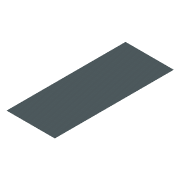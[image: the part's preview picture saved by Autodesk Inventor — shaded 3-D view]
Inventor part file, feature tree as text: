
AUTODESK INVENTOR PART (.ipt)
format: ipt  version: unknown  size: 158,720 bytes
history: native  units: in
note: dims shown in document units (in); Inventor stores cm internally (conversion verified against a paired STEP export)
features: extrude x1, sketch x1
ambient origin geometry x8: Origin, YZ Plane, XZ Plane, XY Plane, X Axis, Y Axis, Z Axis, Center Point
bodies: Solid1 (feature_tree)
feature tree (2):
  extrude  "Extrusion1"  Depth=360.0in
  sketch  "Sketch2"  dims[d0=888.0in d1=360.0in d2=0.25in d3=0.0in]
